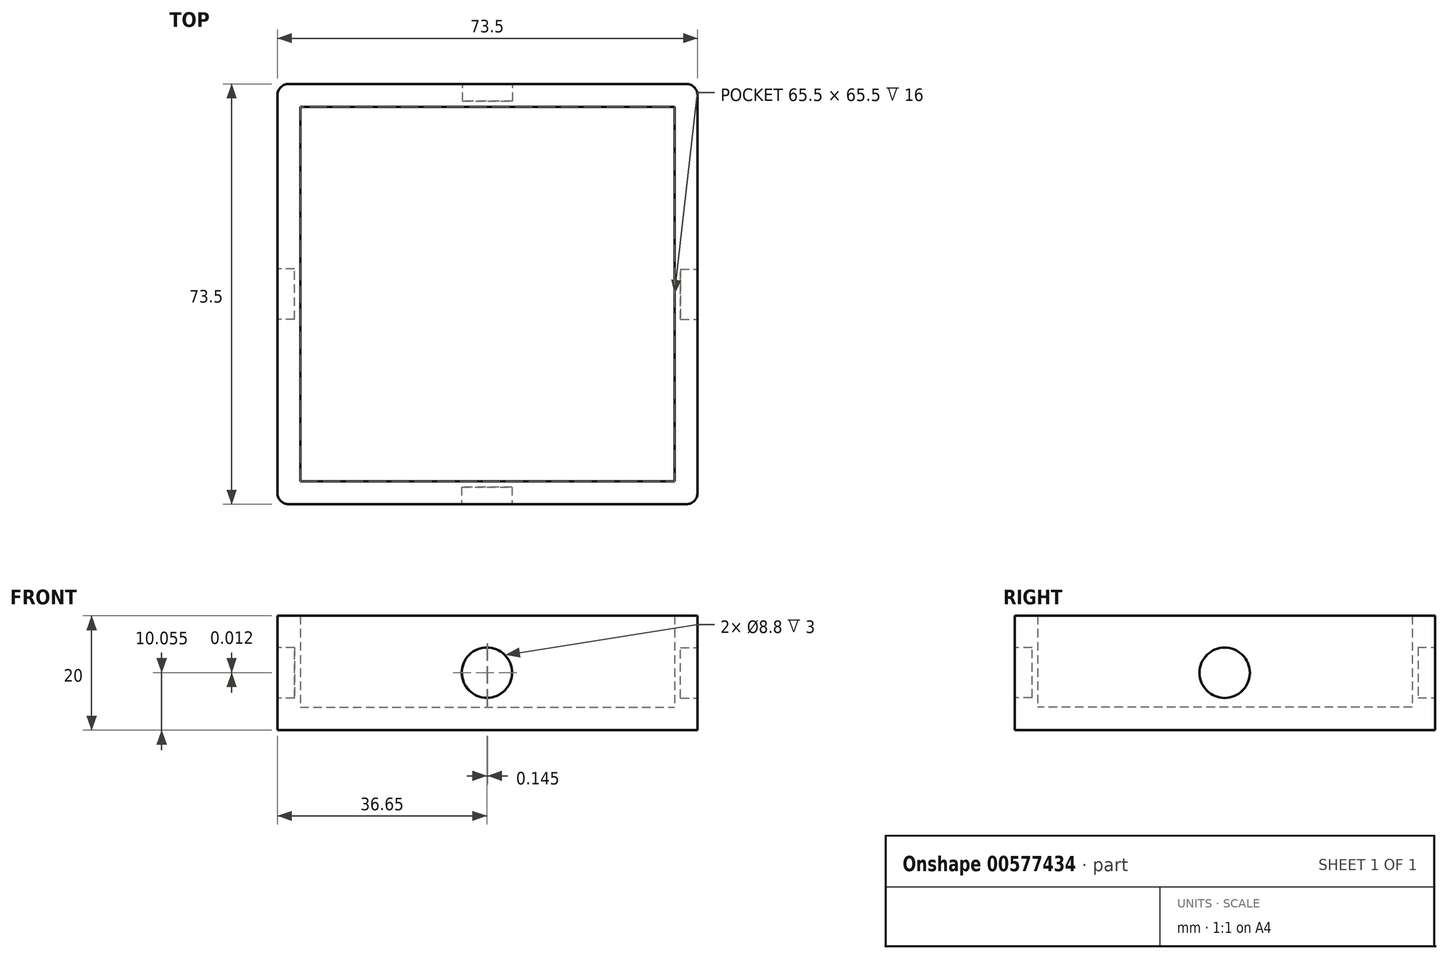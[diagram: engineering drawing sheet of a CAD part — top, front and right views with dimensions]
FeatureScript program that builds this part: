
annotation { "Feature Type Name" : "Feature", "Feature Type Description" : "" }
export const myFeature = defineFeature(function(context is Context, id is Id, definition is map)
    precondition{}
    {
        {
            var Q0;
            Q0=qCreatedBy(makeId("Top.planeOp"),FACE);
            var sketch = newSketch(context, id + "F0", { "sketchPlane" : qUnion([Q0])});
            skLineSegment(sketch, "E0.bottom", {"start": v(-28.45, 28.87) * mm, "end": v(37.05, 28.87) * mm});
            skLineSegment(sketch, "E0.top", {"start": v(-28.45, -36.63) * mm, "end": v(37.05, -36.63) * mm});
            skLineSegment(sketch, "E0.left", {"start": v(-28.45, 28.87) * mm, "end": v(-28.45, -36.63) * mm});
            skLineSegment(sketch, "E0.right", {"start": v(37.05, 28.87) * mm, "end": v(37.05, -36.63) * mm});
            skSolve(sketch);
        }
        {
            var Q0;
            Q0=makeQuery(id+"F0.imprint","IMPRINT",FACE,{"disambiguationData":[TD([[makeQuery(id+"F0.imprint","IMPRINT",EDGE,{"derivedFrom":sQuery(id+"F0.wireOp",EDGE,"E0.bottom")}),-1.0]])]});
            extrude(context, id + "F1", {"entities" : qUnion([Q0]), "depth" : 16 * mm, "offsetDistance" : 25 * mm});
        }
        {
            var Q0;
            Q0=makeQuery(id+"F1.opExtrude","CAP_FACE",FACE,{"disambiguationData":[OSD([sQuery(id+"F0.wireOp",EDGE,"E0.bottom"),sQuery(id+"F0.wireOp",EDGE,"E0.top"),sQuery(id+"F0.wireOp",EDGE,"E0.left"),sQuery(id+"F0.wireOp",EDGE,"E0.right")])],"isStart":false});
            shell(context, id + "F2", {"entities" : qUnion([Q0]), "thickness" : 4 * mm, "oppositeDirection" : true});
        }
        {
            var Q0;
            Q0=makeQuery(id+"F1.opExtrude","SWEPT_EDGE",EDGE,{"disambiguationData":[OSD([sQuery(id+"F0.wireOp",EDGE,"E0.bottom"),sQuery(id+"F0.wireOp",EDGE,"E0.left")])]});
            var Q1;
            Q1=makeQuery(id+"F1.opExtrude","SWEPT_EDGE",EDGE,{"disambiguationData":[OSD([sQuery(id+"F0.wireOp",EDGE,"E0.top"),sQuery(id+"F0.wireOp",EDGE,"E0.left")])]});
            var Q2;
            Q2=makeQuery(id+"F1.opExtrude","SWEPT_EDGE",EDGE,{"disambiguationData":[OSD([sQuery(id+"F0.wireOp",EDGE,"E0.top"),sQuery(id+"F0.wireOp",EDGE,"E0.right")])]});
            var Q3;
            Q3=makeQuery(id+"F1.opExtrude","SWEPT_EDGE",EDGE,{"disambiguationData":[OSD([sQuery(id+"F0.wireOp",EDGE,"E0.bottom"),sQuery(id+"F0.wireOp",EDGE,"E0.right")])]});
            fillet(context, id + "F3", {"entities" : qUnion([Q0, Q1, Q2, Q3]), "radius" : 2 * mm, "tangentPropagation" : true, "allowEdgeOverflow" : false});
        }
        {
            var Q0;
            Q0=makeQuery(id+"F1.opExtrude","SWEPT_FACE",FACE,{"disambiguationData":[OSD([sQuery(id+"F0.wireOp",EDGE,"E0.left")])]});
            var sketch = newSketch(context, id + "F4", { "sketchPlane" : qUnion([Q0])});
            skLineSegment(sketch, "E1", {"start": v(3.88, 16) * mm, "end": v(3.88, -4) * mm, "construction": true});
            skCircle(sketch, "E2", {"center": v(3.88, 6) * mm, "radius": 4.4 * mm});
            skLineSegment(sketch, "E3", {"start": v(38.63, 6) * mm, "end": v(-30.87, 6) * mm, "construction": true});
            skSolve(sketch);
        }
        {
            var Q0;
            Q0=makeQuery(id+"F1.opExtrude","SWEPT_FACE",FACE,{"disambiguationData":[OSD([sQuery(id+"F0.wireOp",EDGE,"E0.top")])]});
            var sketch = newSketch(context, id + "F5", { "sketchPlane" : qUnion([Q0])});
            skCircle(sketch, "E4", {"center": v(4.2, 6.05) * mm, "radius": 4.4 * mm});
            skLineSegment(sketch, "E5", {"start": v(-30.45, 6) * mm, "end": v(39.05, 6) * mm, "construction": true});
            skLineSegment(sketch, "E6", {"start": v(4.3, 16) * mm, "end": v(4.3, -4) * mm, "construction": true});
            skSolve(sketch);
        }
        {
            var Q0;
            Q0=makeQuery(id+"F1.opExtrude","SWEPT_FACE",FACE,{"disambiguationData":[OSD([sQuery(id+"F0.wireOp",EDGE,"E0.right")])]});
            var sketch = newSketch(context, id + "F6", { "sketchPlane" : qUnion([Q0])});
            skCircle(sketch, "E7", {"center": v(-3.93, 6.02) * mm, "radius": 4.4 * mm});
            skSolve(sketch);
        }
        {
            var Q0;
            Q0=makeQuery(id+"F1.opExtrude","SWEPT_FACE",FACE,{"disambiguationData":[OSD([sQuery(id+"F0.wireOp",EDGE,"E0.bottom")])]});
            var sketch = newSketch(context, id + "F7", { "sketchPlane" : qUnion([Q0])});
            skCircle(sketch, "E8", {"center": v(-4.35, 6.07) * mm, "radius": 4.4 * mm});
            skLineSegment(sketch, "E9", {"start": v(30.45, 6) * mm, "end": v(-39.05, 6) * mm, "construction": true});
            skLineSegment(sketch, "E10", {"start": v(-4.3, 16) * mm, "end": v(-4.3, -4) * mm, "construction": true});
            skSolve(sketch);
        }
        {
            var Q0;
            Q0 = qSketchRegion(id + "F4", true);
            extrude(context, id + "F8", {"entities" : qUnion([Q0]), "operationType" : NewBodyOperationType.ADD, "oppositeDirection" : true, "depth" : 3 * mm, "offsetDistance" : 25 * mm});
        }
        {
            var Q0;
            Q0=makeQuery(id+"F4.imprint","IMPRINT",FACE,{"disambiguationData":[TD([[makeQuery(id+"F4.imprint","IMPRINT",EDGE,{"derivedFrom":sQuery(id+"F4.wireOp",EDGE,"E2")}),1.0]])]});
            var Q1;
            Q1=sQuery(id+"F4.wireOp",EDGE,"E2");
            extrude(context, id + "F9", {"entities" : qUnion([Q0]), "operationType" : NewBodyOperationType.REMOVE, "surfaceEntities" : qUnion([Q1]), "oppositeDirection" : true, "depth" : 3 * mm, "offsetDistance" : 25 * mm});
        }
        {
            var Q0;
            Q0=makeQuery(id+"F5.imprint","IMPRINT",FACE,{"disambiguationData":[TD([[makeQuery(id+"F5.imprint","IMPRINT",EDGE,{"derivedFrom":sQuery(id+"F5.wireOp",EDGE,"E4")}),1.0]])]});
            var Q1;
            Q1=sQuery(id+"F5.wireOp",EDGE,"E4");
            extrude(context, id + "F10", {"entities" : qUnion([Q0]), "operationType" : NewBodyOperationType.REMOVE, "surfaceEntities" : qUnion([Q1]), "oppositeDirection" : true, "depth" : 3 * mm, "offsetDistance" : 25 * mm});
        }
        {
            var Q0;
            Q0=makeQuery(id+"F6.imprint","IMPRINT",FACE,{"disambiguationData":[TD([[makeQuery(id+"F6.imprint","IMPRINT",EDGE,{"derivedFrom":sQuery(id+"F6.wireOp",EDGE,"E7")}),1.0]])]});
            extrude(context, id + "F11", {"entities" : qUnion([Q0]), "operationType" : NewBodyOperationType.REMOVE, "oppositeDirection" : true, "depth" : 3 * mm, "offsetDistance" : 25 * mm});
        }
        {
            var Q0;
            Q0=makeQuery(id+"F7.imprint","IMPRINT",FACE,{"disambiguationData":[TD([[makeQuery(id+"F7.imprint","IMPRINT",EDGE,{"derivedFrom":sQuery(id+"F7.wireOp",EDGE,"E8")}),1.0]])]});
            extrude(context, id + "F12", {"entities" : qUnion([Q0]), "operationType" : NewBodyOperationType.REMOVE, "oppositeDirection" : true, "depth" : 3 * mm, "offsetDistance" : 25 * mm});
        }
    });
